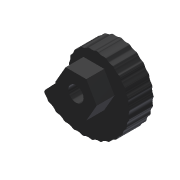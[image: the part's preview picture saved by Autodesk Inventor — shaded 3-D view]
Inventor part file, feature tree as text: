
AUTODESK INVENTOR PART (.ipt)
format: ipt  version: 2013 (Build 170138000, 138)  size: 171,008 bytes
history: native  units: in
note: dims shown in document units (in); Inventor stores cm internally (conversion verified against a paired STEP export)
features: fillet x1, other x1, imported_body x1
ambient origin geometry x8: Origin, YZ Plane, XZ Plane, XY Plane, X Axis, Y Axis, Z Axis, Center Point
feature tree (3):
  fillet  "Fillet1"  [1 undecoded]
  other  "217-3431-STEP1"
  imported_body  "Base1"
note: 1 required parameter value undecoded (feature->parameter linkage not recoverable at this tier; creation-order binding heuristic only, values carry confidence <= 0.55)
